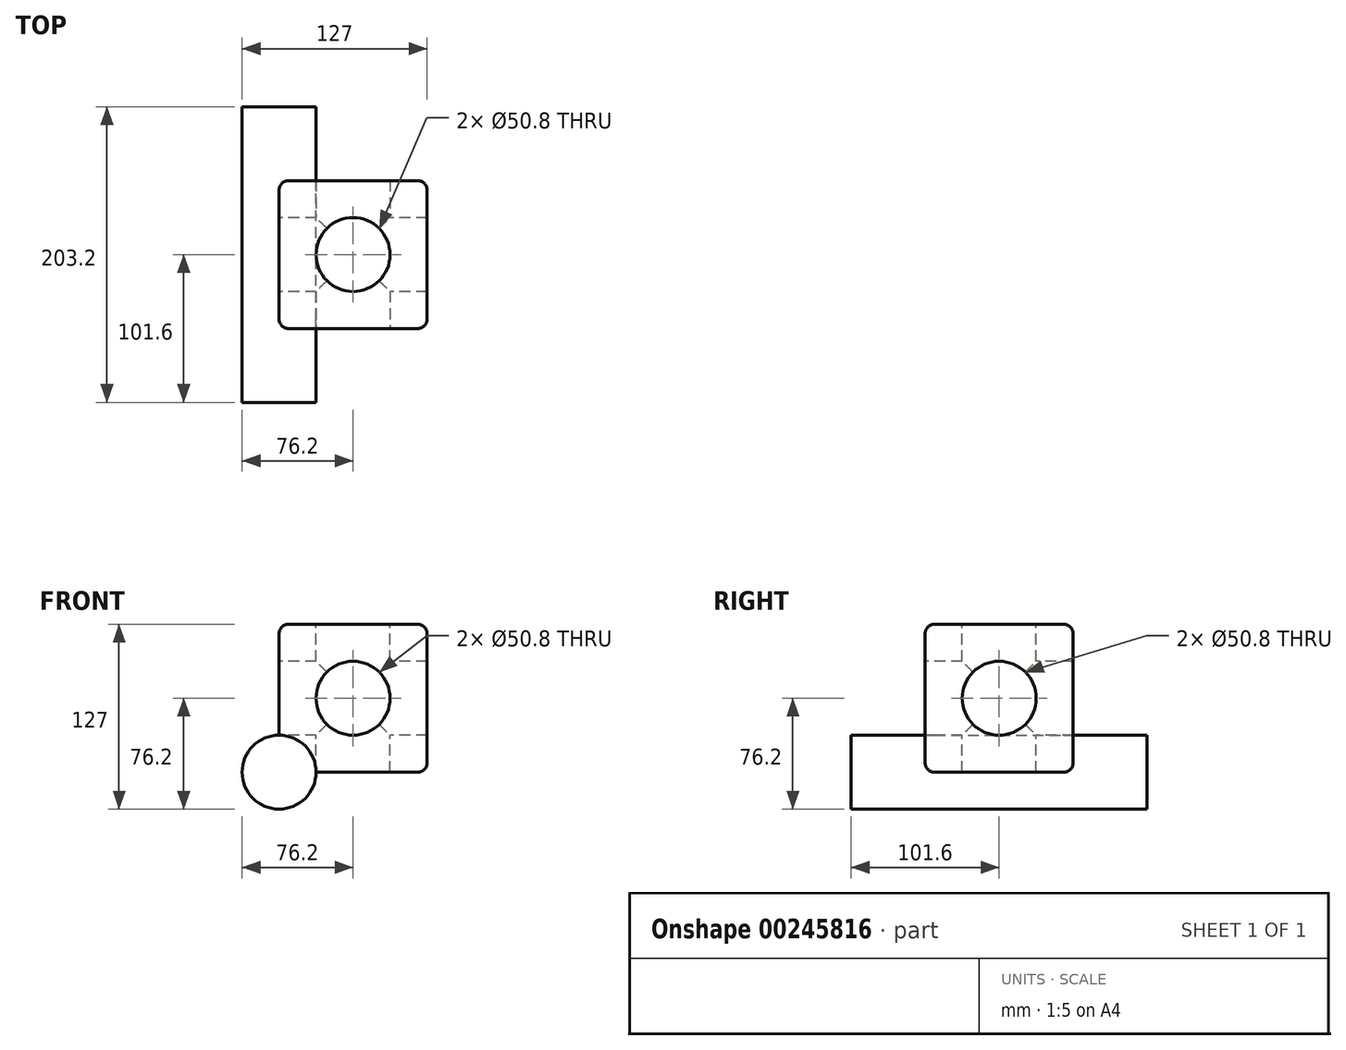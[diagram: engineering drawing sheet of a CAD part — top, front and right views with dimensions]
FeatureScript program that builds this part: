
annotation { "Feature Type Name" : "Feature", "Feature Type Description" : "" }
export const myFeature = defineFeature(function(context is Context, id is Id, definition is map)
    precondition{}
    {
        {
            var Q0;
            Q0=qCreatedBy(makeId("Front.planeOp"),FACE);
            var sketch = newSketch(context, id + "F0", { "sketchPlane" : qUnion([Q0])});
            skLineSegment(sketch, "E0", {"start": v(0, 0) * mm, "end": v(101.6, 0) * mm});
            skLineSegment(sketch, "E1", {"start": v(101.6, 0) * mm, "end": v(101.6, 101.6) * mm});
            skLineSegment(sketch, "E2", {"start": v(101.6, 101.6) * mm, "end": v(0, 101.6) * mm});
            skLineSegment(sketch, "E3", {"start": v(0, 101.6) * mm, "end": v(0, 0) * mm});
            skSolve(sketch);
        }
        {
            var Q0;
            Q0=makeQuery(id+"F0.imprint","IMPRINT",FACE,{"disambiguationData":[TD([[makeQuery(id+"F0.imprint","IMPRINT",EDGE,{"derivedFrom":sQuery(id+"F0.wireOp",EDGE,"E0")}),1.0]])]});
            extrude(context, id + "F1", {"entities" : qUnion([Q0]), "depth" : 101.6 * mm});
        }
        {
            var Q0;
            Q0=makeQuery(id+"F1.opExtrude","SWEPT_FACE",FACE,{"disambiguationData":[OSD([sQuery(id+"F0.wireOp",EDGE,"E2")])]});
            var sketch = newSketch(context, id + "F2", { "sketchPlane" : qUnion([Q0])});
            skCircle(sketch, "E4", {"center": v(50.8, -50.8) * mm, "radius": 25.4 * mm});
            skPoint(sketch, "E5.start.orphan", {"position": v(50.8, 0) * mm});
            skPoint(sketch, "E6.trimOffspring.end.orphan", {"position": v(50.8, -101.6) * mm});
            skSolve(sketch);
        }
        {
            var Q0;
            Q0=makeQuery(id+"F2.imprint","IMPRINT",FACE,{"disambiguationData":[TD([[makeQuery(id+"F2.imprint","IMPRINT",EDGE,{"derivedFrom":sQuery(id+"F2.wireOp",EDGE,"E4")}),1.0]])]});
            extrude(context, id + "F3", {"entities" : qUnion([Q0]), "operationType" : NewBodyOperationType.REMOVE, "oppositeDirection" : true, "depth" : 101.6 * mm});
        }
        {
            var Q0;
            Q0=makeQuery(id+"F1.opExtrude","SWEPT_FACE",FACE,{"disambiguationData":[OSD([sQuery(id+"F0.wireOp",EDGE,"E3")])]});
            var sketch = newSketch(context, id + "F4", { "sketchPlane" : qUnion([Q0])});
            skCircle(sketch, "E7", {"center": v(50.8, 50.8) * mm, "radius": 25.4 * mm});
            skPoint(sketch, "E8.orphan", {"position": v(0, 50.8) * mm});
            skPoint(sketch, "E9.end.orphan", {"position": v(101.6, 50.8) * mm});
            skSolve(sketch);
        }
        {
            var Q0;
            Q0=makeQuery(id+"F4.imprint","IMPRINT",FACE,{"disambiguationData":[TD([[makeQuery(id+"F4.imprint","IMPRINT",EDGE,{"derivedFrom":sQuery(id+"F4.wireOp",EDGE,"E7")}),1.0]])]});
            extrude(context, id + "F5", {"entities" : qUnion([Q0]), "operationType" : NewBodyOperationType.REMOVE, "oppositeDirection" : true, "depth" : 101.6 * mm});
        }
        {
            var Q0;
            Q0=makeQuery(id+"F1.opExtrude","CAP_FACE",FACE,{"disambiguationData":[OSD([sQuery(id+"F0.wireOp",EDGE,"E0"),sQuery(id+"F0.wireOp",EDGE,"E1"),sQuery(id+"F0.wireOp",EDGE,"E2"),sQuery(id+"F0.wireOp",EDGE,"E3")])],"isStart":false});
            var sketch = newSketch(context, id + "F6", { "sketchPlane" : qUnion([Q0])});
            skCircle(sketch, "E10", {"center": v(50.8, 50.8) * mm, "radius": 25.4 * mm});
            skPoint(sketch, "E11.start.orphan", {"position": v(0, 50.8) * mm});
            skPoint(sketch, "E12.trimOffspring.end.orphan", {"position": v(101.6, 50.8) * mm});
            skSolve(sketch);
        }
        {
            var Q0;
            Q0=makeQuery(id+"F6.imprint","IMPRINT",FACE,{"disambiguationData":[TD([[makeQuery(id+"F6.imprint","IMPRINT",EDGE,{"derivedFrom":sQuery(id+"F6.wireOp",EDGE,"E10")}),1.0]])]});
            extrude(context, id + "F7", {"entities" : qUnion([Q0]), "operationType" : NewBodyOperationType.REMOVE, "oppositeDirection" : true, "depth" : 101.6 * mm});
        }
        {
            var Q0;
            Q0=makeQuery(id+"F1.opExtrude","SWEPT_EDGE",EDGE,{"disambiguationData":[OSD([sQuery(id+"F0.wireOp",EDGE,"E2"),sQuery(id+"F0.wireOp",EDGE,"E3")])]});
            var Q1;
            Q1=makeQuery(id+"F1.opExtrude","CAP_EDGE",EDGE,{"disambiguationData":[OSD([sQuery(id+"F0.wireOp",EDGE,"E2")])],"isStart":true});
            var Q2;
            Q2=makeQuery(id+"F1.opExtrude","SWEPT_EDGE",EDGE,{"disambiguationData":[OSD([sQuery(id+"F0.wireOp",EDGE,"E1"),sQuery(id+"F0.wireOp",EDGE,"E2")])]});
            var Q3;
            Q3=makeQuery(id+"F1.opExtrude","CAP_EDGE",EDGE,{"disambiguationData":[OSD([sQuery(id+"F0.wireOp",EDGE,"E2")])],"isStart":false});
            var Q4;
            Q4=makeQuery(id+"F1.opExtrude","CAP_EDGE",EDGE,{"disambiguationData":[OSD([sQuery(id+"F0.wireOp",EDGE,"E3")])],"isStart":false});
            var Q5;
            Q5=makeQuery(id+"F1.opExtrude","CAP_EDGE",EDGE,{"disambiguationData":[OSD([sQuery(id+"F0.wireOp",EDGE,"E1")])],"isStart":false});
            var Q6;
            Q6=makeQuery(id+"F1.opExtrude","CAP_EDGE",EDGE,{"disambiguationData":[OSD([sQuery(id+"F0.wireOp",EDGE,"E1")])],"isStart":true});
            var Q7;
            Q7=makeQuery(id+"F1.opExtrude","SWEPT_EDGE",EDGE,{"disambiguationData":[OSD([sQuery(id+"F0.wireOp",EDGE,"E0"),sQuery(id+"F0.wireOp",EDGE,"E1")])]});
            var Q8;
            Q8=makeQuery(id+"F1.opExtrude","CAP_EDGE",EDGE,{"disambiguationData":[OSD([sQuery(id+"F0.wireOp",EDGE,"E0")])],"isStart":false});
            var Q9;
            Q9=makeQuery(id+"F1.opExtrude","CAP_EDGE",EDGE,{"disambiguationData":[OSD([sQuery(id+"F0.wireOp",EDGE,"E0")])],"isStart":true});
            var Q10;
            Q10=makeQuery(id+"F1.opExtrude","CAP_EDGE",EDGE,{"disambiguationData":[OSD([sQuery(id+"F0.wireOp",EDGE,"E3")])],"isStart":true});
            var Q11;
            Q11=makeQuery(id+"F1.opExtrude","SWEPT_EDGE",EDGE,{"disambiguationData":[OSD([sQuery(id+"F0.wireOp",EDGE,"E0"),sQuery(id+"F0.wireOp",EDGE,"E3")])]});
            fillet(context, id + "F8", {"entities" : qUnion([Q0, Q1, Q2, Q3, Q4, Q5, Q6, Q7, Q8, Q9, Q10, Q11]), "radius" : 6.35 * mm, "tangentPropagation" : true, "allowEdgeOverflow" : false});
        }
        {
            var Q0;
            Q0=qCreatedBy(makeId("Front.planeOp"),FACE);
            cPlane(context, id + "F9", {"entities" : qUnion([Q0]), "cplaneType" : CPlaneType.OFFSET, "offset" : 101.6 * mm, "width" : 152.4 * mm, "height" : 152.4 * mm});
        }
        {
            var Q0;
            Q0=qCreatedBy(id+"F9.planeOp",FACE);
            var sketch = newSketch(context, id + "F10", { "sketchPlane" : qUnion([Q0])});
            skCircle(sketch, "E13", {"center": v(0, 0) * mm, "radius": 25.4 * mm});
            skSolve(sketch);
        }
        {
            var Q0;
            Q0 = qSketchRegion(id + "F10", true);
            extrude(context, id + "F11", {"entities" : qUnion([Q0]), "operationType" : NewBodyOperationType.ADD, "depth" : 50.8 * mm, "hasSecondDirection" : true, "secondDirectionOppositeDirection" : true, "secondDirectionDepth" : 152.4 * mm});
        }
    });
